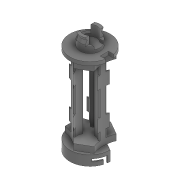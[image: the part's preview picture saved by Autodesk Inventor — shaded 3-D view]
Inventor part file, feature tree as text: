
AUTODESK INVENTOR PART (.ipt)
format: ipt  version: 2022.3 (Build 263350000, 350)  size: 478,208 bytes
history: native  units: mm
features: sketch x18, extrude x16, fillet x2, plane x2, other x1, sweep x1, projected_geometry x1
ambient origin geometry x8: Origin, YZ Plane, XZ Plane, XY Plane, X Axis, Y Axis, Z Axis, Center Point
bodies: Body1 (feature_tree)
feature tree (41):
  other  "Sólido1"
  extrude  "Extrusión1"  Depth=21.0mm
  extrude  "Extrusión2"  Depth=4.6mm
  extrude  "Extrusión3"  Depth=8.0mm TaperAngle=0.0deg
  sweep  "Barrido1"
  extrude  "Extrusión4"  TaperAngle=0.0deg  [1 undecoded]
  extrude  "Extrusión5"  Depth=42.0mm
  extrude  "Extrusión6"  Depth=3.7mm
  extrude  "Extrusión7"  Depth=4.375mm
  extrude  "Extrusión8"  Depth=9.0mm
  fillet  "Empalme1"  Radius=9.0mm
  plane  "Plano de trabajo1"
  extrude  "Extrusión9"  Depth=45.0mm
  plane  "Plano de trabajo2"
  extrude  "Extrusión10"  Depth=3.0mm
  extrude  "Extrusión11"  Depth=3.0mm
  extrude  "Extrusión12"  Depth=68.25mm TaperAngle=0.0deg
  extrude  "Extrusión13"  Depth=8.35mm
  fillet  "Empalme2"  Radius=12.75mm
  extrude  "Extrusión14"  Depth=12.75mm TaperAngle=0.0deg
  extrude  "Extrusión15"  Depth=6.3mm TaperAngle=0.0deg
  extrude  "Extrusión16"  Depth=10.5mm TaperAngle=0.0deg
  sketch  "Boceto1"  dims[d0=21.0mm d1=14.5mm]
  sketch  "Boceto2"  dims[d5=4.6mm d6=8.0mm d7=0.0mm]
  sketch  "Boceto3"  dims[d8=5.0mm d9=5.0mm]
  sketch  "Boceto4"  dims[d10=3.0mm d11=0.0mm d12=0.0mm d13=0.0mm]
  sketch  "Boceto 3D1"  dims[d2=14.0mm d3=0.0mm d4=4.6mm]
  sketch  "Boceto5"  dims[d14=3.0mm d15=0.0mm d16=42.0mm]
  sketch  "Boceto6"  dims[d17=3.7mm d18=0.0mm d19=36.0mm]
  sketch  "Boceto7"  dims[d20=4.375mm d21=4.375mm]
  sketch  "Boceto8"  dims[d22=0.0mm d23=0.0mm d24=9.0mm d25=9.0mm]
  sketch  "Boceto9"  dims[d26=45.0mm d27=45.0mm]
  sketch  "Boceto10"  dims[d28=45.0mm d29=3.0mm]
  sketch  "Boceto11"  dims[d30=3.0mm d31=3.0mm]
  sketch  "Boceto13"  dims[d32=6.3mm d33=0.0mm]
  sketch  "Boceto14"  dims[d34=9.0mm d35=9.0mm d36=45.0mm d37=45.0mm d38=45.0mm d39=3.0mm d40=3.0mm d41=3.0mm d42=68.25mm d43=0.0mm]
  sketch  "Boceto15"  dims[d44=1.0mm d45=8.35mm]
  sketch  "Boceto16"  dims[d46=9.0mm d47=9.0mm d48=45.0mm d49=45.0mm d50=45.0mm d51=3.0mm d52=3.0mm d53=3.0mm d54=12.75mm d55=0.0mm]
  sketch  "Boceto17"  dims[d56=47.25mm]
  sketch  "Boceto18"  dims[d57=9.0mm d58=9.0mm d59=45.0mm d60=45.0mm d61=45.0mm d62=3.0mm d63=3.0mm d64=3.0mm d65=12.75mm d66=0.0mm d67=6.3mm d68=0.0mm d69=10.5mm d70=0.0mm d71=40.0mm d72=14.0mm d73=1.0mm d74=6.8mm d75=0.0mm d76=0.15mm d77=3.0mm d78=6.8mm d79=0.0mm d80=3.0mm d81=1.0mm d82=3.5mm d83=0.0mm d84=0.0mm d85=9.0mm d86=9.0mm d87=2.5mm d88=0.0mm d89=14.25mm d90=4.0mm d91=9.0mm]
  projected_geometry  "Contorno proyectado2"
note: 1 required parameter value undecoded (feature->parameter linkage not recoverable at this tier; creation-order binding heuristic only, values carry confidence <= 0.55)
